# Revit family: Shower_Bar-GROHE-Tempesta_Rustic-27519_Series
name_source: partatom
category: Specialty Equipment
revit_build: Autodesk Revit 2014 (Build: 20130308_1515(x64)
units: mm (PartAtom-declared; Revit-internal decimal feet)

## types (2) — shared parameters
Assembly Code = D2010710
CalGreen Compliant = Yes
Cold Water Connection Diameter = 1/2"
Cold Water Connection Radius = 1/4"
Default Elevation = 78"
Description = Tempesta Rustic 24" Shower Bar
Hot Water Connection Diameter = 1"
Hot Water Connection Radius = 1/4"
Installation Type = Wall Mounted
Length = 3 3/16"
Manufacturer = Grohe
Price = Prices may vary. Please consult Manufacturer Representative for most up-to-date price list.
Product Page URL = https://www.grohe.us
Tempered Connection Diameter = 1/2"
Tempered Connection Radius = 1/4"
URL = https://www.grohe.us
Warranty Documentation Link = https://cdn.cloud.grohe.com
Width = 2 7/8"
cUPC Compliant = Yes

## per-type parameters (varying)
| type | Finish | Height | Material |
| 27519000 | Metal-Grohe-000-Chrome | 24 13/32" | Metal-Grohe-000-Chrome |
| 27519EN0 | Metal-Grohe-EN0-Brushed Nickel | 30 5/16" | Metal-Grohe-EN0-Brushed Nickel |

note: column(s) folded — value = type name in every type: Model

## geometry (parser evidence)
native form markers: Sweep x3
no freeform markers — native parametric forms only
